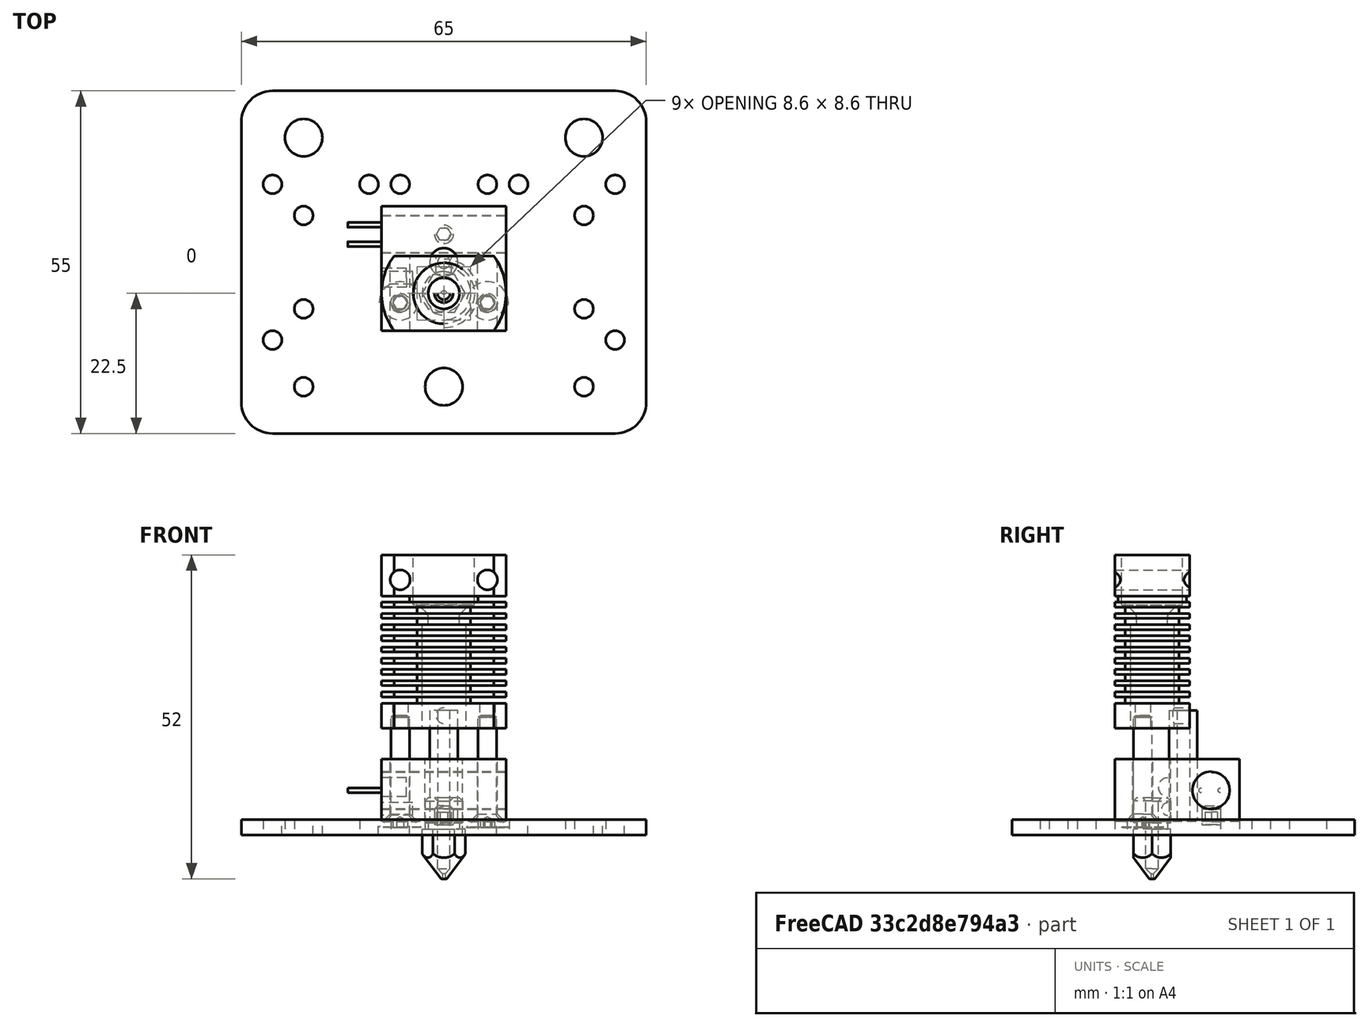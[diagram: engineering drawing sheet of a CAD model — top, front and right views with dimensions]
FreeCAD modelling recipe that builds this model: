
FCSTD DOCUMENT  (FreeCAD 0.19R24276 (Git))
Label: hotend
License: All rights reserved
LicenseURL: http://en.wikipedia.org/wiki/All_rights_reserved
objects: App::FeaturePython×43, Part::FeaturePython×35, Part::Feature×8, Sketcher::SketchObject×1, PartDesign::FeatureBase×1, PartDesign::Pad×1, PartDesign::Body×1
note: 47 computed .brp shape members not serialized (recipe doc carries the construction recipe); baked Part::Feature solids carry a one-line shape summary decoded from their .brp

FEATURE [Part::Feature] Part__Feature  label="Heat block"
  Placement = pos=(2.95042e-06,-1.00001,2.2) rot=(-0.577355,-0.577345,0.577351;0rad)
  shape: bbox 20 x 20 x 10 mm, 26 faces (baked)
FEATURE [Part::Feature] Part__Feature001  label="Heater"
  Placement = pos=(-10,4.49999,7.2) rot=(0,1,0;1.5708rad)
  shape: bbox 25.42 x 5.9 x 5.9 mm, 10 faces (baked)
FEATURE [Part::Feature] Part__Feature002  label="Radiator"
  Placement = pos=(8.76188e-07,-5,41) rot=(0.707107,0.707107,0;3.14159rad)
  shape: bbox 20 x 12 x 27.8 mm, 110 faces (baked)
FEATURE [Part::Feature] Part__Feature003  label="HotendPlate"
  shape: bbox 65 x 55 x 2.5 mm, 27 faces (baked)
FEATURE [Part::Feature] Part__Feature004  label="blockScreww"
  Placement = pos=(-7,-6.50001,19.2) rot=(0.577678,0.576695,0.577678;4.18781rad)
  shape: bbox 6.721 x 6.721 x 18 mm, 27 faces (baked)
FEATURE [Part::Feature] Part__Feature006  label="blockScrew02"
  Placement = pos=(7,-6.5,19.2) rot=(0.602638,0.523121,0.602638;4.10554rad)
  shape: bbox 6.721 x 6.721 x 18 mm, 27 faces (baked)
FEATURE [Part::Feature] Part__Feature007  label="M3 Screw"
  Placement = pos=(2.65241e-06,4.49999,1.7) rot=(1,0,0;1.5708rad)
  shape: bbox 3 x 3 x 3 mm, 13 faces (baked)
FEATURE [Part::Feature] Part__Feature008  label="nozzle"
  Placement = pos=(3.26037e-06,-5.00001,1) rot=(0,1,0;3.14159rad)
  shape: bbox 6.929 x 6.929 x 13 mm, 26 faces (baked)
FEATURE [Part::FeaturePython] Parts  # WARN: FeaturePython — macro-defined, semantics opaque (R4)
  Group = -> [Origin,Part__Feature,Part__Feature001,Part__Feature002,Part__Feature004,Part__Feature006,Part__Feature007,Part__Feature008]
  GroupMode = 0
FEATURE [Sketcher::SketchObject] Sketch
  FullyConstrained = true
  MapMode = 5
  Support = -> [XY_Plane001]
  sketch-geometry (2):
    g0: Circle CenterX=0 CenterY=0 CenterZ=0 NormalX=0 NormalY=0 NormalZ=1 AngleXU=0 Radius=2.25
    g1: Circle CenterX=0 CenterY=0 CenterZ=0 NormalX=0 NormalY=0 NormalZ=1 AngleXU=0 Radius=1
  constraints (4):
    c: Coincident(g1,g0)
    c: Diameter(g0) = 4.5
    c: Diameter(g1) = 2
    c: Coincident(g0,g-1)
FEATURE [PartDesign::FeatureBase] BaseFeature
  BaseFeature = -> Part__Feature003
FEATURE [PartDesign::Pad] Pad
  BaseFeature = -> BaseFeature
  Direction = (1,1,1)
  Length = 20
  Length2 = 100
  Profile = -> Sketch
  Type = 0
FEATURE [PartDesign::Body] Body
  BaseFeature = -> Part__Feature003
  Group = -> [BaseFeature,Sketch,Pad]
  Origin = -> Origin001
  Tip = -> Pad
FEATURE [Part::FeaturePython] Assembly  # WARN: FeaturePython — macro-defined, semantics opaque (R4)
  AutoRelax = true
  BuildShape = 0
  Freeze = false
  Group = -> [Constraints,Elements,Parts]
  Verbose = false
  _SolverType = 1
  _Version = 1
FEATURE [App::FeaturePython] Constraints  # WARN: FeaturePython — macro-defined, semantics opaque (R4)
  Group = -> [Constraint,Constraint003,Constraint004,Constraint005,Constraint006,Constraint007,Constraint008,Constraint009,Constraint010,Constraint011,Constraint012,Constraint013,Constraint014,Constraint015]
  _Version = 1
FEATURE [App::FeaturePython] Elements  # WARN: FeaturePython — macro-defined, semantics opaque (R4)
  Group = -> [_Element,_Element001,_Element002,_Element003,_Element004,_Element005,_Element006,_Element007,_Element008,_Element009,_Element010,_Element011,_Element012,_Element013,_Element014,_Element015,_Element016,_Element017,_Element018,_Element019,_Element020,_Element021,_Element022,_Element023,_Element024,_Element025,_Element026,_Element027,_Element028,_Element029,_Element030,_Element031,_Element032]
FEATURE [Part::FeaturePython] _Element  # link proxy (typed FeaturePython)
  Detach = false
  LinkTransform = true
  LinkedObject = -> Part__Feature002 [Face46]
  _Parent = -> Elements
FEATURE [Part::FeaturePython] _Element001  # link proxy (typed FeaturePython)
  Detach = false
  LinkTransform = true
  LinkedObject = -> Part__Feature [Edge37]
  _Parent = -> Elements
FEATURE [Part::FeaturePython] _Element002  # link proxy (typed FeaturePython)
  Detach = false
  LinkTransform = true
  LinkedObject = -> Part__Feature002 [Edge20]
  _Parent = -> Elements
FEATURE [Part::FeaturePython] _Element003  # link proxy (typed FeaturePython)
  Detach = false
  LinkTransform = true
  LinkedObject = -> Part__Feature [Edge6]
  _Parent = -> Elements
FEATURE [Part::FeaturePython] _Element004  # link proxy (typed FeaturePython)
  Detach = false
  LinkTransform = true
  LinkedObject = -> Part__Feature002 [Edge101]
  _Parent = -> Elements
FEATURE [Part::FeaturePython] _Element005  # link proxy (typed FeaturePython)
  Detach = false
  LinkTransform = true
  LinkedObject = -> Part__Feature [Edge2]
  _Parent = -> Elements
FEATURE [Part::FeaturePython] _Element006  # link proxy (typed FeaturePython)
  Detach = false
  LinkTransform = true
  LinkedObject = -> Part__Feature [Edge36]
  _Parent = -> Elements
FEATURE [Part::FeaturePython] _Element007  # link proxy (typed FeaturePython)
  Detach = false
  LinkTransform = true
  LinkedObject = -> Part__Feature002 [Edge100]
  _Parent = -> Elements
FEATURE [Part::FeaturePython] _Element008  # link proxy (typed FeaturePython)
  Detach = false
  LinkTransform = true
  LinkedObject = -> Part__Feature002 [Edge16]
  _Parent = -> Elements
FEATURE [App::FeaturePython] Constraint  label="Locked"  # WARN: FeaturePython — macro-defined, semantics opaque (R4)
  Disabled = false
  Group = -> [ElementLink]
  _ConstraintType = 0
  _Parent = -> Constraints
FEATURE [App::FeaturePython] ElementLink  label="_Element"  # link proxy (typed FeaturePython)
  LinkTransform = true
  LinkedObject = -> _Element
  _Parent = -> Constraint
FEATURE [Part::FeaturePython] _Element009  # link proxy (typed FeaturePython)
  Detach = false
  LinkTransform = true
  LinkedObject = -> Part__Feature004 [Face27]
  _Parent = -> Elements
FEATURE [Part::FeaturePython] _Element010  # link proxy (typed FeaturePython)
  Detach = false
  LinkTransform = true
  LinkedObject = -> Part__Feature006 [Face27]
  _Parent = -> Elements
FEATURE [App::FeaturePython] Constraint003  label="AxialAlignment002"  # WARN: FeaturePython — macro-defined, semantics opaque (R4)
  Angle = 0
  AnglePitch = 0
  AngleRoll = 0
  Disabled = false
  Group = -> [ElementLink005,ElementLink006]
  LockAngle = false
  Multiply = false
  _ConstraintType = 36
  _Parent = -> Constraints
FEATURE [App::FeaturePython] ElementLink005  label="_Element009"  # link proxy (typed FeaturePython)
  LinkTransform = true
  LinkedObject = -> _Element009
  _Parent = -> Constraint003
FEATURE [App::FeaturePython] ElementLink006  label="_Element008"  # link proxy (typed FeaturePython)
  LinkTransform = true
  LinkedObject = -> _Element008
  _Parent = -> Constraint003
FEATURE [App::FeaturePython] Constraint004  label="AxialAlignment003"  # WARN: FeaturePython — macro-defined, semantics opaque (R4)
  Angle = 0
  AnglePitch = 0
  AngleRoll = 0
  Disabled = false
  Group = -> [ElementLink007,ElementLink008]
  LockAngle = false
  Multiply = false
  _ConstraintType = 36
  _Parent = -> Constraints
FEATURE [App::FeaturePython] ElementLink007  label="_Element002"  # link proxy (typed FeaturePython)
  LinkTransform = true
  LinkedObject = -> _Element002
  _Parent = -> Constraint004
FEATURE [App::FeaturePython] ElementLink008  label="_Element010"  # link proxy (typed FeaturePython)
  LinkTransform = true
  LinkedObject = -> _Element010
  _Parent = -> Constraint004
FEATURE [Part::FeaturePython] _Element011  # link proxy (typed FeaturePython)
  Detach = false
  LinkTransform = true
  LinkedObject = -> Part__Feature004 [Edge27]
  _Parent = -> Elements
FEATURE [Part::FeaturePython] _Element012  # link proxy (typed FeaturePython)
  Detach = false
  LinkTransform = true
  LinkedObject = -> Part__Feature [Edge43]
  _Parent = -> Elements
FEATURE [Part::FeaturePython] _Element013  # link proxy (typed FeaturePython)
  Detach = false
  LinkTransform = true
  LinkedObject = -> Part__Feature006 [Edge27]
  _Parent = -> Elements
FEATURE [Part::FeaturePython] _Element014  # link proxy (typed FeaturePython)
  Detach = false
  LinkTransform = true
  LinkedObject = -> Part__Feature [Edge44]
  _Parent = -> Elements
FEATURE [Part::FeaturePython] _Element015  # link proxy (typed FeaturePython)
  Detach = false
  LinkTransform = true
  LinkedObject = -> Part__Feature004 [Edge20]
  _Parent = -> Elements
FEATURE [Part::FeaturePython] _Element016  # link proxy (typed FeaturePython)
  Detach = false
  LinkTransform = true
  LinkedObject = -> Part__Feature006 [Edge20]
  _Parent = -> Elements
FEATURE [App::FeaturePython] Constraint005  label="AxialAlignment"  # WARN: FeaturePython — macro-defined, semantics opaque (R4)
  Angle = 0
  AnglePitch = 0
  AngleRoll = 0
  Disabled = false
  Group = -> [ElementLink009,ElementLink010]
  LockAngle = false
  Multiply = false
  _ConstraintType = 36
  _Parent = -> Constraints
FEATURE [App::FeaturePython] ElementLink009  label="_Element009"  # link proxy (typed FeaturePython)
  LinkTransform = true
  LinkedObject = -> _Element009
  _Parent = -> Constraint005
FEATURE [App::FeaturePython] ElementLink010  label="_Element005"  # link proxy (typed FeaturePython)
  LinkTransform = true
  LinkedObject = -> _Element005
  _Parent = -> Constraint005
FEATURE [App::FeaturePython] Constraint006  label="AxialAlignment004"  # WARN: FeaturePython — macro-defined, semantics opaque (R4)
  Angle = 0
  AnglePitch = 0
  AngleRoll = 0
  Disabled = false
  Group = -> [ElementLink011,ElementLink012]
  LockAngle = false
  Multiply = false
  _ConstraintType = 36
  _Parent = -> Constraints
FEATURE [App::FeaturePython] ElementLink011  label="_Element010"  # link proxy (typed FeaturePython)
  LinkTransform = true
  LinkedObject = -> _Element010
  _Parent = -> Constraint006
FEATURE [App::FeaturePython] ElementLink012  label="_Element001"  # link proxy (typed FeaturePython)
  LinkTransform = true
  LinkedObject = -> _Element001
  _Parent = -> Constraint006
FEATURE [App::FeaturePython] Constraint007  label="PointsPlaneDistance"  # WARN: FeaturePython — macro-defined, semantics opaque (R4)
  Disabled = false
  Distance = -1
  Group = -> [ElementLink013,ElementLink014]
  _ConstraintType = 7
  _Parent = -> Constraints
FEATURE [App::FeaturePython] ElementLink013  label="_Element017"  # link proxy (typed FeaturePython)
  LinkTransform = true
  LinkedObject = -> _Element017
  _Parent = -> Constraint007
FEATURE [Part::FeaturePython] _Element017  # link proxy (typed FeaturePython)
  Detach = false
  LinkTransform = true
  LinkedObject = -> Part__Feature004 [Edge24]
  _Parent = -> Elements
FEATURE [App::FeaturePython] ElementLink014  label="_Element018"  # link proxy (typed FeaturePython)
  LinkTransform = true
  LinkedObject = -> _Element018
  _Parent = -> Constraint007
FEATURE [Part::FeaturePython] _Element018  # link proxy (typed FeaturePython)
  Detach = false
  LinkTransform = true
  LinkedObject = -> Part__Feature [Face20]
  _Parent = -> Elements
FEATURE [App::FeaturePython] Constraint008  label="PointsPlaneDistance001"  # WARN: FeaturePython — macro-defined, semantics opaque (R4)
  Disabled = false
  Distance = 1
  Group = -> [ElementLink015,ElementLink016]
  _ConstraintType = 7
  _Parent = -> Constraints
FEATURE [App::FeaturePython] ElementLink015  label="_Element018"  # link proxy (typed FeaturePython)
  LinkTransform = true
  LinkedObject = -> _Element018
  _Parent = -> Constraint008
FEATURE [App::FeaturePython] ElementLink016  label="_Element019"  # link proxy (typed FeaturePython)
  LinkTransform = true
  LinkedObject = -> _Element019
  _Parent = -> Constraint008
FEATURE [Part::FeaturePython] _Element019  # link proxy (typed FeaturePython)
  Detach = false
  LinkTransform = true
  LinkedObject = -> Part__Feature006 [Edge24]
  _Parent = -> Elements
FEATURE [Part::FeaturePython] _Element020  # link proxy (typed FeaturePython)
  Detach = false
  LinkTransform = true
  LinkedObject = -> Part__Feature007 [Face4]
  _Parent = -> Elements
FEATURE [App::FeaturePython] Constraint009  label="AxialAlignment005"  # WARN: FeaturePython — macro-defined, semantics opaque (R4)
  Angle = 0
  AnglePitch = 0
  AngleRoll = 0
  Disabled = false
  Group = -> [ElementLink017,ElementLink018]
  LockAngle = false
  Multiply = false
  _ConstraintType = 36
  _Parent = -> Constraints
FEATURE [App::FeaturePython] ElementLink017  label="_Element021"  # link proxy (typed FeaturePython)
  LinkTransform = true
  LinkedObject = -> _Element021
  _Parent = -> Constraint009
FEATURE [Part::FeaturePython] _Element021  # link proxy (typed FeaturePython)
  Detach = false
  LinkTransform = true
  LinkedObject = -> Part__Feature [Edge60]
  _Parent = -> Elements
FEATURE [App::FeaturePython] ElementLink018  label="_Element020"  # link proxy (typed FeaturePython)
  LinkTransform = true
  LinkedObject = -> _Element020
  _Parent = -> Constraint009
FEATURE [App::FeaturePython] Constraint010  label="PointsPlaneDistance002"  # WARN: FeaturePython — macro-defined, semantics opaque (R4)
  Disabled = false
  Distance = 0.5
  Group = -> [ElementLink019,ElementLink020]
  _ConstraintType = 7
  _Parent = -> Constraints
FEATURE [App::FeaturePython] ElementLink019  label="_Element018"  # link proxy (typed FeaturePython)
  LinkTransform = true
  LinkedObject = -> _Element018
  _Parent = -> Constraint010
FEATURE [App::FeaturePython] ElementLink020  label="_Element022"  # link proxy (typed FeaturePython)
  LinkTransform = true
  LinkedObject = -> _Element022
  _Parent = -> Constraint010
FEATURE [Part::FeaturePython] _Element022  # link proxy (typed FeaturePython)
  Detach = false
  LinkTransform = true
  LinkedObject = -> Part__Feature007 [Edge9]
  _Parent = -> Elements
FEATURE [App::FeaturePython] Constraint011  label="AxialAlignment006"  # WARN: FeaturePython — macro-defined, semantics opaque (R4)
  Angle = 0
  AnglePitch = 0
  AngleRoll = 0
  Disabled = false
  Group = -> [ElementLink021,ElementLink022]
  LockAngle = false
  Multiply = false
  _ConstraintType = 36
  _Parent = -> Constraints
FEATURE [App::FeaturePython] ElementLink021  label="_Element023"  # link proxy (typed FeaturePython)
  LinkTransform = true
  LinkedObject = -> _Element023
  _Parent = -> Constraint011
FEATURE [Part::FeaturePython] _Element023  # link proxy (typed FeaturePython)
  Detach = false
  LinkTransform = true
  LinkedObject = -> Part__Feature001 [Face4]
  _Parent = -> Elements
FEATURE [App::FeaturePython] ElementLink022  label="_Element024"  # link proxy (typed FeaturePython)
  LinkTransform = true
  LinkedObject = -> _Element024
  _Parent = -> Constraint011
FEATURE [Part::FeaturePython] _Element024  # link proxy (typed FeaturePython)
  Detach = false
  LinkTransform = true
  LinkedObject = -> Part__Feature [Edge54]
  _Parent = -> Elements
FEATURE [App::FeaturePython] Constraint012  label="PointsPlaneDistance003"  # WARN: FeaturePython — macro-defined, semantics opaque (R4)
  Disabled = false
  Distance = 0
  Group = -> [ElementLink023,ElementLink024]
  _ConstraintType = 7
  _Parent = -> Constraints
FEATURE [App::FeaturePython] ElementLink023  label="_Element025"  # link proxy (typed FeaturePython)
  LinkTransform = true
  LinkedObject = -> _Element025
  _Parent = -> Constraint012
FEATURE [Part::FeaturePython] _Element025  # link proxy (typed FeaturePython)
  Detach = false
  LinkTransform = true
  LinkedObject = -> Part__Feature001 [Edge8]
  _Parent = -> Elements
FEATURE [App::FeaturePython] ElementLink024  label="_Element026"  # link proxy (typed FeaturePython)
  LinkTransform = true
  LinkedObject = -> _Element026
  _Parent = -> Constraint012
FEATURE [Part::FeaturePython] _Element026  # link proxy (typed FeaturePython)
  Detach = false
  LinkTransform = true
  LinkedObject = -> Part__Feature [Face16]
  _Parent = -> Elements
FEATURE [App::FeaturePython] Constraint013  label="PointsPlaneDistance004"  # WARN: FeaturePython — macro-defined, semantics opaque (R4)
  Disabled = false
  Distance = 5
  Group = -> [ElementLink025,ElementLink026]
  _ConstraintType = 7
  _Parent = -> Constraints
FEATURE [App::FeaturePython] ElementLink025  label="_Element027"  # link proxy (typed FeaturePython)
  LinkTransform = true
  LinkedObject = -> _Element027
  _Parent = -> Constraint013
FEATURE [Part::FeaturePython] _Element027  # link proxy (typed FeaturePython)
  Detach = false
  LinkTransform = true
  LinkedObject = -> Part__Feature002 [Face24]
  _Parent = -> Elements
FEATURE [App::FeaturePython] ElementLink026  label="_Element028"  # link proxy (typed FeaturePython)
  LinkTransform = true
  LinkedObject = -> _Element028
  _Parent = -> Constraint013
FEATURE [Part::FeaturePython] _Element028  # link proxy (typed FeaturePython)
  Detach = false
  LinkTransform = true
  LinkedObject = -> Part__Feature [Face10]
  _Parent = -> Elements
FEATURE [App::FeaturePython] Constraint014  label="AxialAlignment007"  # WARN: FeaturePython — macro-defined, semantics opaque (R4)
  Angle = 0
  AnglePitch = 0
  AngleRoll = 0
  Disabled = false
  Group = -> [ElementLink027,ElementLink028]
  LockAngle = false
  Multiply = false
  _ConstraintType = 36
  _Parent = -> Constraints
FEATURE [App::FeaturePython] ElementLink027  label="_Element029"  # link proxy (typed FeaturePython)
  LinkTransform = true
  LinkedObject = -> _Element029
  _Parent = -> Constraint014
FEATURE [Part::FeaturePython] _Element029  # link proxy (typed FeaturePython)
  Detach = false
  LinkTransform = true
  LinkedObject = -> Part__Feature008 [Face20]
  _Parent = -> Elements
FEATURE [App::FeaturePython] ElementLink028  label="_Element030"  # link proxy (typed FeaturePython)
  LinkTransform = true
  LinkedObject = -> _Element030
  _Parent = -> Constraint014
FEATURE [Part::FeaturePython] _Element030  # link proxy (typed FeaturePython)
  Detach = false
  LinkTransform = true
  LinkedObject = -> Part__Feature [Edge45]
  _Parent = -> Elements
FEATURE [App::FeaturePython] Constraint015  label="AxialAlignment008"  # WARN: FeaturePython — macro-defined, semantics opaque (R4)
  Angle = 0
  AnglePitch = 0
  AngleRoll = 0
  Disabled = false
  Group = -> [ElementLink029,ElementLink030]
  LockAngle = false
  Multiply = false
  _ConstraintType = 36
  _Parent = -> Constraints
FEATURE [App::FeaturePython] ElementLink029  label="_Element031"  # link proxy (typed FeaturePython)
  LinkTransform = true
  LinkedObject = -> _Element031
  _Parent = -> Constraint015
FEATURE [Part::FeaturePython] _Element031  # WARN: FeaturePython — macro-defined, semantics opaque (R4)
  Detach = false
  LinkTransform = true
  _Parent = -> Elements
FEATURE [App::FeaturePython] ElementLink030  label="_Element032"  # link proxy (typed FeaturePython)
  LinkTransform = true
  LinkedObject = -> _Element032
  _Parent = -> Constraint015
FEATURE [Part::FeaturePython] _Element032  # link proxy (typed FeaturePython)
  Detach = false
  LinkTransform = true
  LinkedObject = -> Part__Feature002 [Edge41]
  _Parent = -> Elements
